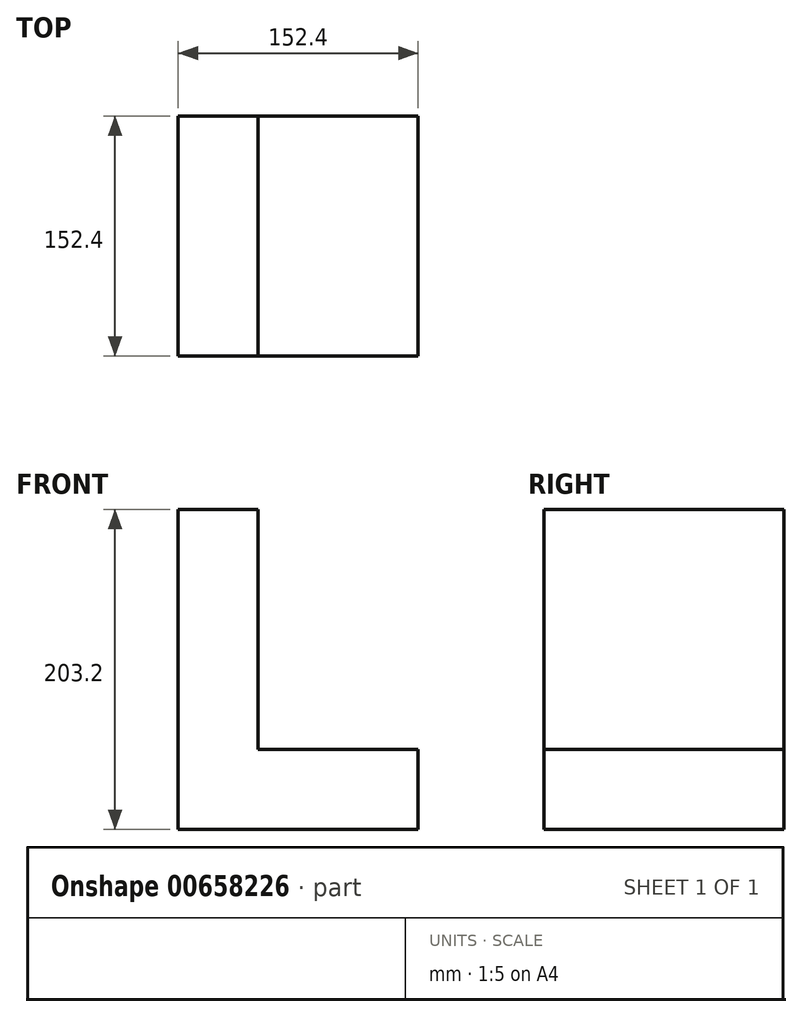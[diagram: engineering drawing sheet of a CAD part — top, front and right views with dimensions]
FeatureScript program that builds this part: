
annotation { "Feature Type Name" : "Feature", "Feature Type Description" : "" }
export const myFeature = defineFeature(function(context is Context, id is Id, definition is map)
    precondition{}
    {
        {
            var Q0;
            Q0=qCreatedBy(makeId("Front.planeOp"),FACE);
            var sketch = newSketch(context, id + "F0", { "sketchPlane" : qUnion([Q0])});
            skLineSegment(sketch, "E0", {"start": v(0, 0) * mm, "end": v(0, -203.2) * mm});
            skLineSegment(sketch, "E1", {"start": v(0, -203.2) * mm, "end": v(152.4, -203.2) * mm});
            skLineSegment(sketch, "E2", {"start": v(152.4, -203.2) * mm, "end": v(152.4, -152.4) * mm});
            skLineSegment(sketch, "E3", {"start": v(0, 0) * mm, "end": v(50.8, 0) * mm});
            skLineSegment(sketch, "E4", {"start": v(50.8, 0) * mm, "end": v(50.8, -152.4) * mm});
            skLineSegment(sketch, "E5", {"start": v(50.8, -152.4) * mm, "end": v(152.4, -152.4) * mm});
            skSolve(sketch);
        }
        {
            var Q0;
            Q0=makeQuery(id+"F0.imprint","IMPRINT",FACE,{"disambiguationData":[TD([[makeQuery(id+"F0.imprint","IMPRINT",EDGE,{"derivedFrom":sQuery(id+"F0.wireOp",EDGE,"E0")}),1.0]])]});
            var Q1;
            Q1 = qSketchRegion(id + "FD7icTGZqQ0Gepd_0", true);
            extrude(context, id + "F1", {"entities" : qUnion([Q0, Q1]), "depth" : 152.4 * mm, "offsetDistance" : 25.4 * mm});
        }
    });
